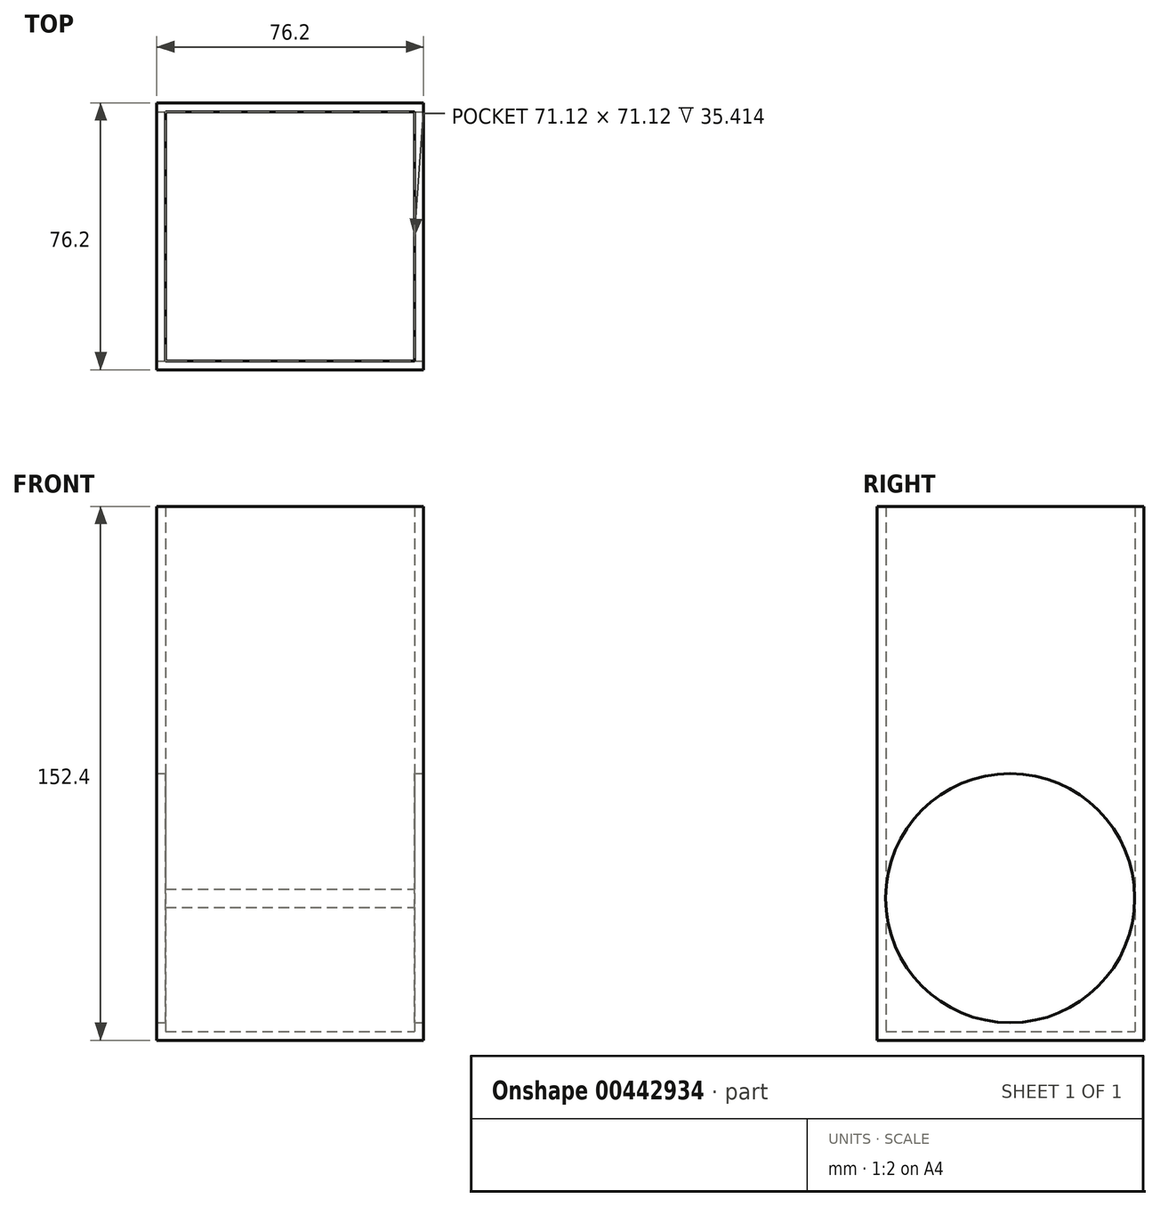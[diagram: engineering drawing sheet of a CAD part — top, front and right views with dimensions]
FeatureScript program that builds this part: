
annotation { "Feature Type Name" : "Feature", "Feature Type Description" : "" }
export const myFeature = defineFeature(function(context is Context, id is Id, definition is map)
    precondition{}
    {
        {
            var Q0;
            Q0=qCreatedBy(makeId("Front.planeOp"),FACE);
            var sketch = newSketch(context, id + "F0", { "sketchPlane" : qUnion([Q0])});
            skLineSegment(sketch, "E0.bottom", {"start": v(-24.84, -40.57) * mm, "end": v(51.36, -40.57) * mm});
            skLineSegment(sketch, "E0.top", {"start": v(-24.84, 111.83) * mm, "end": v(51.36, 111.83) * mm});
            skLineSegment(sketch, "E0.left", {"start": v(-24.84, -40.57) * mm, "end": v(-24.84, 111.83) * mm});
            skLineSegment(sketch, "E0.right", {"start": v(51.36, -40.57) * mm, "end": v(51.36, 111.83) * mm});
            skPoint(sketch, "E0.middle", {"position": v(13.26, 35.63) * mm});
            skSolve(sketch);
        }
        {
            var Q0;
            Q0=makeQuery(id+"F0.imprint","IMPRINT",FACE,{"disambiguationData":[TD([[makeQuery(id+"F0.imprint","IMPRINT",EDGE,{"derivedFrom":sQuery(id+"F0.wireOp",EDGE,"E0.bottom")}),1.0]])]});
            extrude(context, id + "F1", {"entities" : qUnion([Q0]), "depth" : 2.54 * mm});
        }
        {
            var Q0;
            Q0=makeQuery(id+"F1.opExtrude","CAP_FACE",FACE,{"disambiguationData":[OSD([sQuery(id+"F0.wireOp",EDGE,"E0.bottom"),sQuery(id+"F0.wireOp",EDGE,"E0.top"),sQuery(id+"F0.wireOp",EDGE,"E0.left"),sQuery(id+"F0.wireOp",EDGE,"E0.right")])],"isStart":false});
            var sketch = newSketch(context, id + "F2", { "sketchPlane" : qUnion([Q0])});
            skLineSegment(sketch, "E1.bottom", {"start": v(-24.84, 111.83) * mm, "end": v(-22.3, 111.83) * mm});
            skLineSegment(sketch, "E1.top", {"start": v(-24.84, -40.57) * mm, "end": v(-22.3, -40.57) * mm});
            skLineSegment(sketch, "E1.left", {"start": v(-24.84, 111.83) * mm, "end": v(-24.84, -40.57) * mm});
            skLineSegment(sketch, "E1.right", {"start": v(-22.3, 111.83) * mm, "end": v(-22.3, -40.57) * mm});
            skLineSegment(sketch, "E2.bottom", {"start": v(51.36, 111.83) * mm, "end": v(48.82, 111.83) * mm});
            skLineSegment(sketch, "E2.top", {"start": v(51.36, -40.57) * mm, "end": v(48.82, -40.57) * mm});
            skLineSegment(sketch, "E2.left", {"start": v(51.36, 111.83) * mm, "end": v(51.36, -40.57) * mm});
            skLineSegment(sketch, "E2.right", {"start": v(48.82, 111.83) * mm, "end": v(48.82, -40.57) * mm});
            skLineSegment(sketch, "E3.bottom", {"start": v(-22.3, -40.57) * mm, "end": v(48.82, -40.57) * mm});
            skLineSegment(sketch, "E3.top", {"start": v(-22.3, -38.03) * mm, "end": v(48.82, -38.03) * mm});
            skLineSegment(sketch, "E3.left", {"start": v(-22.3, -40.57) * mm, "end": v(-22.3, -38.03) * mm});
            skLineSegment(sketch, "E3.right", {"start": v(48.82, -40.57) * mm, "end": v(48.82, -38.03) * mm});
            skSolve(sketch);
        }
        {
            var Q0;
            Q0=makeQuery(id+"F2.imprint","IMPRINT",FACE,{"disambiguationData":[TD([[makeQuery(id+"F2.imprint","IMPRINT",EDGE,{"derivedFrom":sQuery(id+"F2.wireOp",EDGE,"E1.bottom")}),-1.0]])]});
            var Q1;
            Q1=makeQuery(id+"F2.imprint","IMPRINT",FACE,{"disambiguationData":[TD([[makeQuery(id+"F2.imprint","IMPRINT",EDGE,{"derivedFrom":sQuery(id+"F2.wireOp",EDGE,"E3.bottom")}),1.0]])]});
            var Q2;
            Q2=makeQuery(id+"F2.imprint","IMPRINT",FACE,{"disambiguationData":[TD([[makeQuery(id+"F2.imprint","IMPRINT",EDGE,{"derivedFrom":sQuery(id+"F2.wireOp",EDGE,"E2.bottom")}),-1.0]])]});
            extrude(context, id + "F3", {"entities" : qUnion([Q0, Q1, Q2]), "operationType" : NewBodyOperationType.ADD, "depth" : 73.66 * mm});
        }
        {
            var Q0;
            Q0=makeQuery(id+"F3.opExtrude","CAP_FACE",FACE,{"disambiguationData":[OSD([sQuery(id+"F2.wireOp",EDGE,"E1.bottom"),sQuery(id+"F2.wireOp",EDGE,"E1.top"),sQuery(id+"F2.wireOp",EDGE,"E1.left"),sQuery(id+"F2.wireOp",EDGE,"E1.right"),sQuery(id+"F2.wireOp",EDGE,"E2.bottom"),sQuery(id+"F2.wireOp",EDGE,"E2.top"),sQuery(id+"F2.wireOp",EDGE,"E2.left"),sQuery(id+"F2.wireOp",EDGE,"E2.right"),sQuery(id+"F2.wireOp",EDGE,"E3.bottom"),sQuery(id+"F2.wireOp",EDGE,"E3.top")])],"isStart":false});
            var sketch = newSketch(context, id + "F4", { "sketchPlane" : qUnion([Q0])});
            skLineSegment(sketch, "E4.bottom", {"start": v(-24.84, -40.57) * mm, "end": v(51.36, -40.57) * mm});
            skLineSegment(sketch, "E4.top", {"start": v(-24.84, 111.83) * mm, "end": v(51.36, 111.83) * mm});
            skLineSegment(sketch, "E4.left", {"start": v(-24.84, -40.57) * mm, "end": v(-24.84, 111.83) * mm});
            skLineSegment(sketch, "E4.right", {"start": v(51.36, -40.57) * mm, "end": v(51.36, 111.83) * mm});
            skSolve(sketch);
        }
        {
            var Q0;
            {var subQ1=makeQuery(id+"F3.opExtrude","CAP_EDGE",EDGE,{"disambiguationData":[OSD([sQuery(id+"F2.wireOp",EDGE,"E1.right")])],"isStart":false});Q0=makeQuery(id+"F4.imprint","IMPRINT",FACE,{"disambiguationData":[TD([[makeQuery(id+"F4.imprint","IMPRINT",EDGE,{"derivedFrom":subQ1}),1.0]])]});}
            extrude(context, id + "F5", {"entities" : qUnion([Q0]), "operationType" : NewBodyOperationType.ADD, "oppositeDirection" : true, "depth" : 2.54 * mm});
        }
        {
            var Q0;
            Q0=makeQuery(id+"F3.boolean.opBoolean","MERGE",FACE,{"derivedFrom":[makeQuery(id+"F1.opExtrude","SWEPT_FACE",FACE,{"disambiguationData":[OSD([sQuery(id+"F0.wireOp",EDGE,"E0.right")])]}),makeQuery(id+"F3.opExtrude","SWEPT_FACE",FACE,{"disambiguationData":[OSD([sQuery(id+"F2.wireOp",EDGE,"E2.left")])]})]});
            var sketch = newSketch(context, id + "F6", { "sketchPlane" : qUnion([Q0])});
            skCircle(sketch, "E5", {"center": v(-38.2, 0) * mm, "radius": 35.56 * mm});
            skSolve(sketch);
        }
        {
            var Q0;
            {var subQ0=sQuery(id+"F6.wireOp",EDGE,"E5");var subQ1=makeQuery(id+"F1.opExtrude","CAP_EDGE",EDGE,{"disambiguationData":[OSD([sQuery(id+"F0.wireOp",EDGE,"E0.right")])],"isStart":true});var subQ2=makeQuery(id+"F6.imprint","INTERSECT",VERTEX,{"disambiguationData":[OD(0.0)],"derivedFrom":[subQ1,subQ0]});Q0=makeQuery(id+"F6.imprint","IMPRINT",FACE,{"disambiguationData":[TD([[makeQuery(id+"F6.imprint","IMPRINT",EDGE,{"disambiguationData":[TD([[subQ2,1.0]])],"derivedFrom":subQ0}),1.0]])]});}
            extrude(context, id + "F7", {"entities" : qUnion([Q0]), "operationType" : NewBodyOperationType.REMOVE, "oppositeDirection" : true, "depth" : 101.6 * mm});
        }
    });
